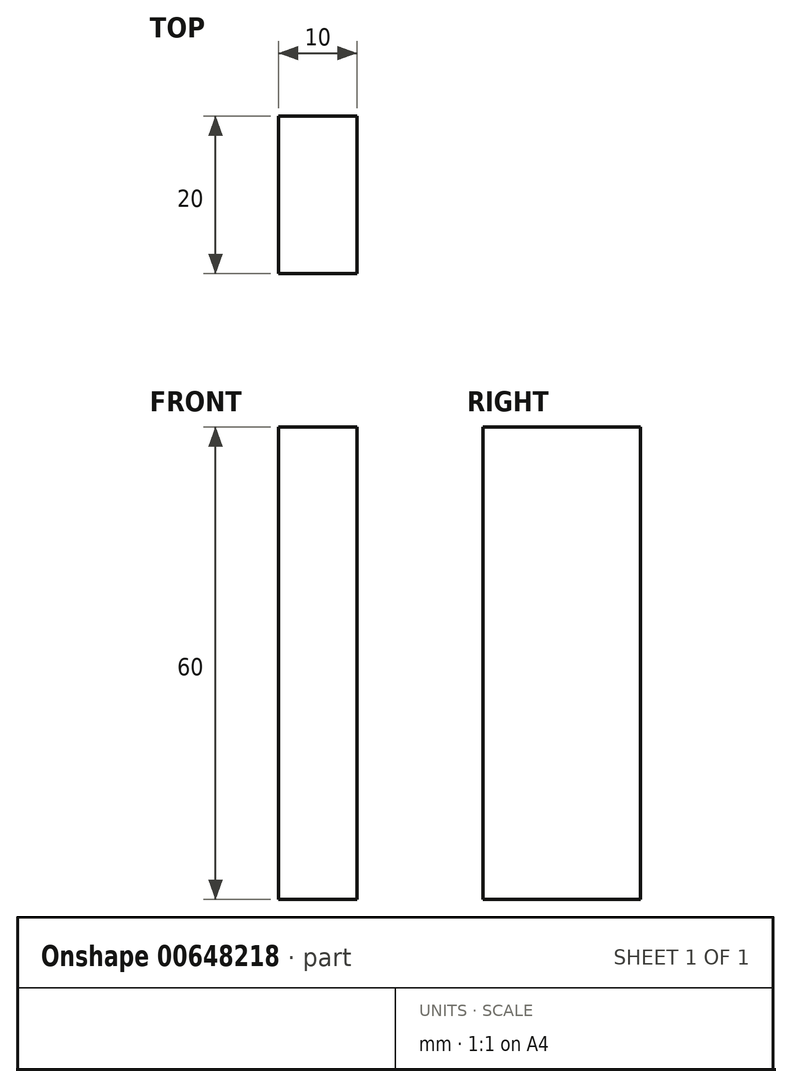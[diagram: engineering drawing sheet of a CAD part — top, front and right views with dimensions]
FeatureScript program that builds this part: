
annotation { "Feature Type Name" : "Feature", "Feature Type Description" : "" }
export const myFeature = defineFeature(function(context is Context, id is Id, definition is map)
    precondition{}
    {
        {
            var Q0;
            Q0=qCreatedBy(makeId("Top.planeOp"),FACE);
            var sketch = newSketch(context, id + "F0", { "sketchPlane" : qUnion([Q0])});
            skLineSegment(sketch, "E0.bottom", {"start": v(0, 0) * mm, "end": v(10, 0) * mm});
            skLineSegment(sketch, "E0.top", {"start": v(0, 20) * mm, "end": v(10, 20) * mm});
            skLineSegment(sketch, "E0.left", {"start": v(0, 0) * mm, "end": v(0, 20) * mm});
            skLineSegment(sketch, "E0.right", {"start": v(10, 0) * mm, "end": v(10, 20) * mm});
            skSolve(sketch);
        }
        {
            var Q0;
            Q0 = qSketchRegion(id + "F0", true);
            extrude(context, id + "F1", {"entities" : qUnion([Q0]), "depth" : 60 * mm, "offsetDistance" : 25 * mm});
        }
    });
